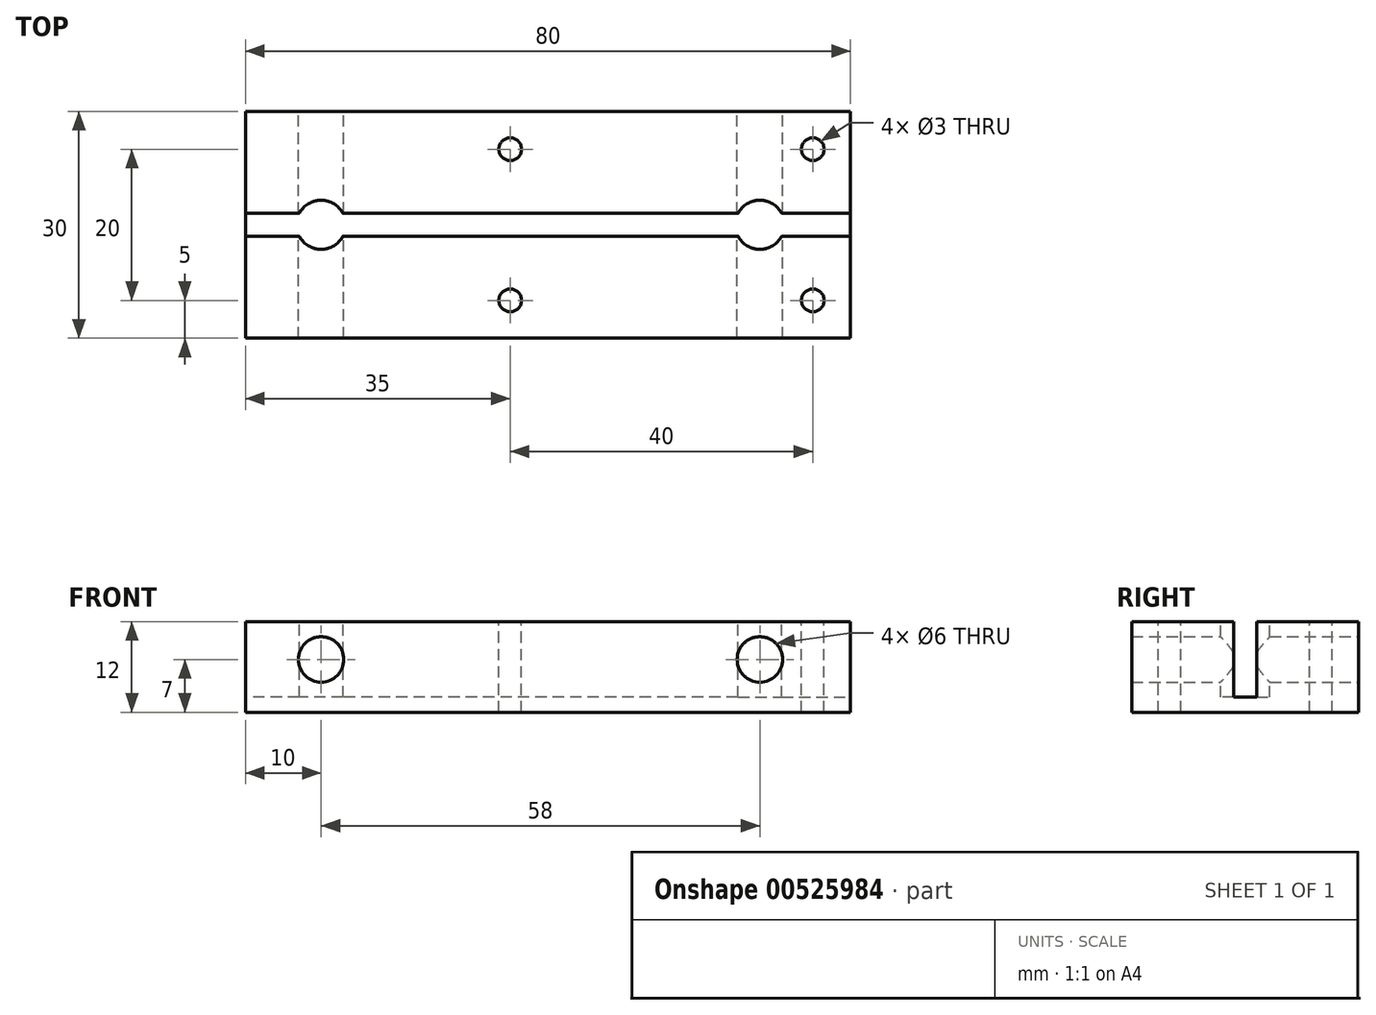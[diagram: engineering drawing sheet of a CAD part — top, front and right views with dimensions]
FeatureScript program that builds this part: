
annotation { "Feature Type Name" : "Feature", "Feature Type Description" : "" }
export const myFeature = defineFeature(function(context is Context, id is Id, definition is map)
    precondition{}
    {
        {
            var Q0;
            Q0=qCreatedBy(makeId("Top.planeOp"),FACE);
            var sketch = newSketch(context, id + "F0", { "sketchPlane" : qUnion([Q0])});
            skLineSegment(sketch, "E0.bottom", {"start": v(0, 0) * mm, "end": v(80, 0) * mm});
            skLineSegment(sketch, "E0.top", {"start": v(0, 30) * mm, "end": v(80, 30) * mm});
            skLineSegment(sketch, "E0.left", {"start": v(0, 0) * mm, "end": v(0, 30) * mm});
            skLineSegment(sketch, "E0.right", {"start": v(80, 0) * mm, "end": v(80, 30) * mm});
            skSolve(sketch);
        }
        {
            var Q0;
            Q0 = qSketchRegion(id + "F0", true);
            extrude(context, id + "F1", {"entities" : qUnion([Q0]), "depth" : 12 * mm, "offsetDistance" : 25 * mm});
        }
        {
            var Q0;
            {var subQ3=sQuery(id+"F0.wireOp",EDGE,"E0.left");var subQ4=sQuery(id+"F0.wireOp",EDGE,"E0.right");var subQ5=sQuery(id+"F0.wireOp",EDGE,"E0.bottom");Q0=makeQuery(id+"FnWeHgFp6HXiUen_1.boolean.opBoolean","SPLIT",FACE,{"disambiguationData":[TD([makeQuery(id+"F1.opExtrude","SWEPT_FACE",FACE,{"disambiguationData":[OSD([subQ5])]})])],"derivedFrom":makeQuery(id+"F1.opExtrude","CAP_FACE",FACE,{"disambiguationData":[OSD([subQ5,sQuery(id+"F0.wireOp",EDGE,"E0.top"),subQ3,subQ4])],"isStart":false})});}
            var sketch = newSketch(context, id + "F2", { "sketchPlane" : qUnion([Q0])});
            skLineSegment(sketch, "E1", {"start": v(30, 5) * mm, "end": v(80, 5) * mm, "construction": true});
            skCircle(sketch, "E2", {"center": v(35, 5) * mm, "radius": 1.5 * mm});
            skCircle(sketch, "E3.0.1.0", {"center": v(35, 25) * mm, "radius": 1.5 * mm});
            skCircle(sketch, "E3.1.0.0", {"center": v(75, 5) * mm, "radius": 1.5 * mm});
            skCircle(sketch, "E3.1.1.0", {"center": v(75, 25) * mm, "radius": 1.5 * mm});
            skLineSegment(sketch, "E3.direction1", {"start": v(35, 5) * mm, "end": v(75, 5) * mm, "construction": true});
            skLineSegment(sketch, "E3.direction2", {"start": v(35, 5) * mm, "end": v(35, 25) * mm, "construction": true});
            skSolve(sketch);
        }
        {
            var Q0;
            Q0 = qSketchRegion(id + "F2", true);
            extrude(context, id + "F3", {"entities" : qUnion([Q0]), "operationType" : NewBodyOperationType.REMOVE, "oppositeDirection" : true, "depth" : 25 * mm, "offsetDistance" : 25 * mm});
        }
        {
            var Q0;
            Q0=makeQuery(id+"F1.opExtrude","CAP_FACE",FACE,{"disambiguationData":[OSD([sQuery(id+"F0.wireOp",EDGE,"E0.bottom"),sQuery(id+"F0.wireOp",EDGE,"E0.top"),sQuery(id+"F0.wireOp",EDGE,"E0.left"),sQuery(id+"F0.wireOp",EDGE,"E0.right")])],"isStart":false});
            var sketch = newSketch(context, id + "F4", { "sketchPlane" : qUnion([Q0])});
            skLineSegment(sketch, "E4", {"start": v(0, 15) * mm, "end": v(80, 15) * mm, "construction": true});
            skLineSegment(sketch, "E5", {"start": v(10, 30) * mm, "end": v(10, 0) * mm, "construction": true});
            skLineSegment(sketch, "E6", {"start": v(68, 30) * mm, "end": v(68, 0) * mm, "construction": true});
            skArc(sketch, "E7", {"start": v(65.12, 13.5) * mm, "mid": v(68, 11.75) * mm, "end": v(70.88, 13.5) * mm});
            skArc(sketch, "E8", {"start": v(12.88, 16.5) * mm, "mid": v(10, 18.25) * mm, "end": v(7.12, 16.5) * mm});
            skPoint(sketch, "E9.visualSharp", {"position": v(15.75, 19.25) * mm});
            skPoint(sketch, "E10.visualSharp", {"position": v(15.75, 10.75) * mm});
            skPoint(sketch, "E11.visualSharp", {"position": v(42.75, 16.75) * mm});
            skPoint(sketch, "E12.visualSharp", {"position": v(42.75, 13.25) * mm});
            skPoint(sketch, "E13.orphan", {"position": v(13.1, 16) * mm});
            skPoint(sketch, "E14.start.orphan", {"position": v(13.1, 14) * mm});
            skLineSegment(sketch, "E15", {"start": v(80, 16.5) * mm, "end": v(70.88, 16.5) * mm});
            skLineSegment(sketch, "E16", {"start": v(0, 13.5) * mm, "end": v(7.12, 13.5) * mm});
            skLineSegment(sketch, "E17", {"start": v(80, 13.5) * mm, "end": v(80, 16.5) * mm});
            skLineSegment(sketch, "E18", {"start": v(0, 13.5) * mm, "end": v(0, 16.5) * mm});
            skArc(sketch, "E19.trimOffspring", {"start": v(7.12, 13.5) * mm, "mid": v(10, 11.75) * mm, "end": v(12.88, 13.5) * mm});
            skArc(sketch, "E20.trimOffspring", {"start": v(70.88, 16.5) * mm, "mid": v(68, 18.25) * mm, "end": v(65.12, 16.5) * mm});
            skLineSegment(sketch, "E21.trimOffspring", {"start": v(70.88, 13.5) * mm, "end": v(80, 13.5) * mm});
            skLineSegment(sketch, "E22.trimOffspring", {"start": v(65.12, 16.5) * mm, "end": v(42.82, 16.5) * mm});
            skLineSegment(sketch, "E23.trimOffspring", {"start": v(7.12, 16.5) * mm, "end": v(0, 16.5) * mm});
            skLineSegment(sketch, "E24.trimOffspring", {"start": v(12.88, 13.5) * mm, "end": v(65.12, 13.5) * mm});
            skLineSegment(sketch, "E25.trimOffspring", {"start": v(42.82, 13.5) * mm, "end": v(65.12, 13.5) * mm});
            skLineSegment(sketch, "E26.trimOffspring", {"start": v(65.12, 16.5) * mm, "end": v(12.88, 16.5) * mm});
            skSolve(sketch);
        }
        {
            var Q0;
            Q0=makeQuery(id+"F4.imprint","IMPRINT",FACE,{"disambiguationData":[TD([[makeQuery(id+"F4.imprint","IMPRINT",EDGE,{"derivedFrom":sQuery(id+"F4.wireOp",EDGE,"E8")}),1.0]])]});
            extrude(context, id + "F5", {"entities" : qUnion([Q0]), "operationType" : NewBodyOperationType.REMOVE, "oppositeDirection" : true, "depth" : 5 * mm, "offsetDistance" : 25 * mm});
        }
        {
            var Q0;
            {var subQ0=sQuery(id+"F4.wireOp",EDGE,"E8");var subQ1=makeQuery(id+"F4.imprint","INTERSECT",VERTEX,{"derivedFrom":[subQ0,sQuery(id+"F4.wireOp",EDGE,"1d010f7b-b8ef-4790-a1ea-6a26900cbe5c.trimOffspring")]});Q0=makeQuery(id+"F4.imprint","IMPRINT",FACE,{"disambiguationData":[TD([[makeQuery(id+"F4.imprint","IMPRINT",EDGE,{"disambiguationData":[TD([[subQ1,-1.0]])],"derivedFrom":subQ0}),1.0]])]});}
            extrude(context, id + "F6", {"entities" : qUnion([Q0]), "operationType" : NewBodyOperationType.REMOVE, "oppositeDirection" : true, "depth" : 10 * mm, "offsetDistance" : 25 * mm});
        }
        {
            var Q0;
            Q0=makeQuery(id+"F1.opExtrude","SWEPT_FACE",FACE,{"disambiguationData":[OSD([sQuery(id+"F0.wireOp",EDGE,"E0.top")])]});
            var sketch = newSketch(context, id + "F7", { "sketchPlane" : qUnion([Q0])});
            skCircle(sketch, "E27", {"center": v(-68, 7) * mm, "radius": 3 * mm});
            skCircle(sketch, "E28", {"center": v(-10, 7) * mm, "radius": 3 * mm});
            skLineSegment(sketch, "E29", {"start": v(-80, 7) * mm, "end": v(0, 7) * mm, "construction": true});
            skSolve(sketch);
        }
        {
            var Q0;
            Q0 = qSketchRegion(id + "F7", true);
            var Q1;
            Q1=makeQuery(id+"FjxfviPTMP6CY7n_1.boolean.opBoolean","COPY",FACE,{"derivedFrom":makeQuery(id+"FjxfviPTMP6CY7n_1.opExtrude","SWEPT_FACE",FACE,{"disambiguationData":[OSD([sQuery(id+"F4.wireOp",EDGE,"VoHIX8aj-H2fN-NTHB-Hb94-qxzSb2CF8Wn6")])]})});
            extrude(context, id + "F8", {"entities" : qUnion([Q0]), "operationType" : NewBodyOperationType.REMOVE, "endBound" : BoundingType.THROUGH_ALL, "oppositeDirection" : true, "depth" : 15 * mm, "endBoundEntityFace" : qUnion([Q1]), "offsetDistance" : 25 * mm});
        }
    });
